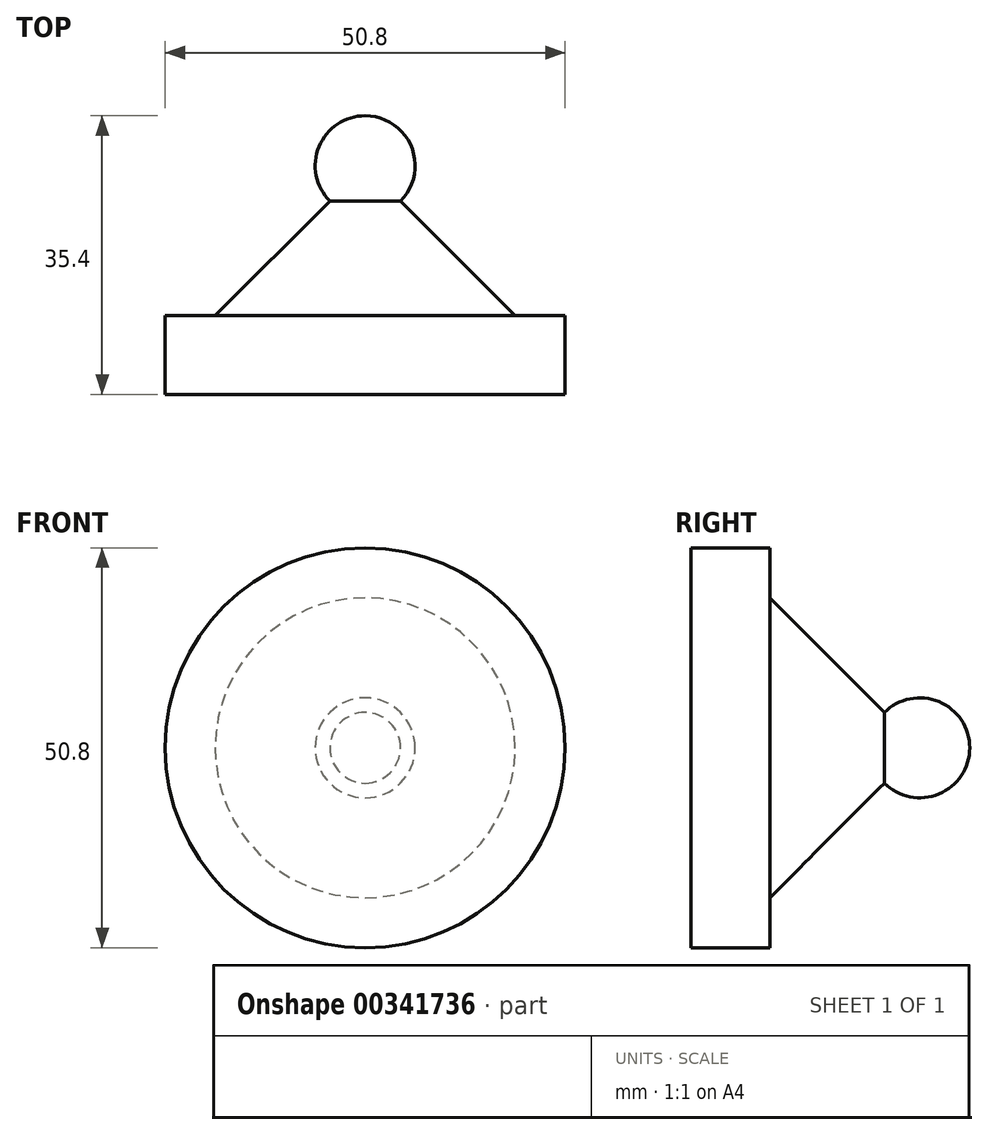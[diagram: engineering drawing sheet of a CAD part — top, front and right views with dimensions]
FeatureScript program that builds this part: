
annotation { "Feature Type Name" : "Feature", "Feature Type Description" : "" }
export const myFeature = defineFeature(function(context is Context, id is Id, definition is map)
    precondition{}
    {
        {
            var Q0;
            Q0=qCreatedBy(makeId("Top.planeOp"),FACE);
            var sketch = newSketch(context, id + "F0", { "sketchPlane" : qUnion([Q0])});
            skLineSegment(sketch, "E0", {"start": v(0, 0) * mm, "end": v(0, 29.05) * mm});
            skLineSegment(sketch, "E1", {"start": v(0, 0) * mm, "end": v(-25.4, 0) * mm});
            skLineSegment(sketch, "E2", {"start": v(-25.4, 0) * mm, "end": v(-25.4, 10) * mm});
            skLineSegment(sketch, "E3", {"start": v(-25.4, 10) * mm, "end": v(-19.05, 10) * mm});
            skLineSegment(sketch, "E4", {"start": v(-19.05, 10) * mm, "end": v(0, 29.05) * mm});
            skArc(sketch, "E5", {"start": v(0, 35.4) * mm, "mid": v(-5.87, 31.48) * mm, "end": v(-4.5, 24.56) * mm});
            skLineSegment(sketch, "E6", {"start": v(0, 35.4) * mm, "end": v(0, 29.05) * mm});
            skSolve(sketch);
        }
        {
            var Q0;
            Q0 = qSketchRegion(id + "F0", true);
            var Q1;
            Q1=sQuery(id+"F0.wireOp",EDGE,"E0");
            revolve(context, id + "F1", {"entities" : qUnion([Q0]), "axis" : qUnion([Q1]), "revolveType" : RevolveType.FULL});
        }
    });
